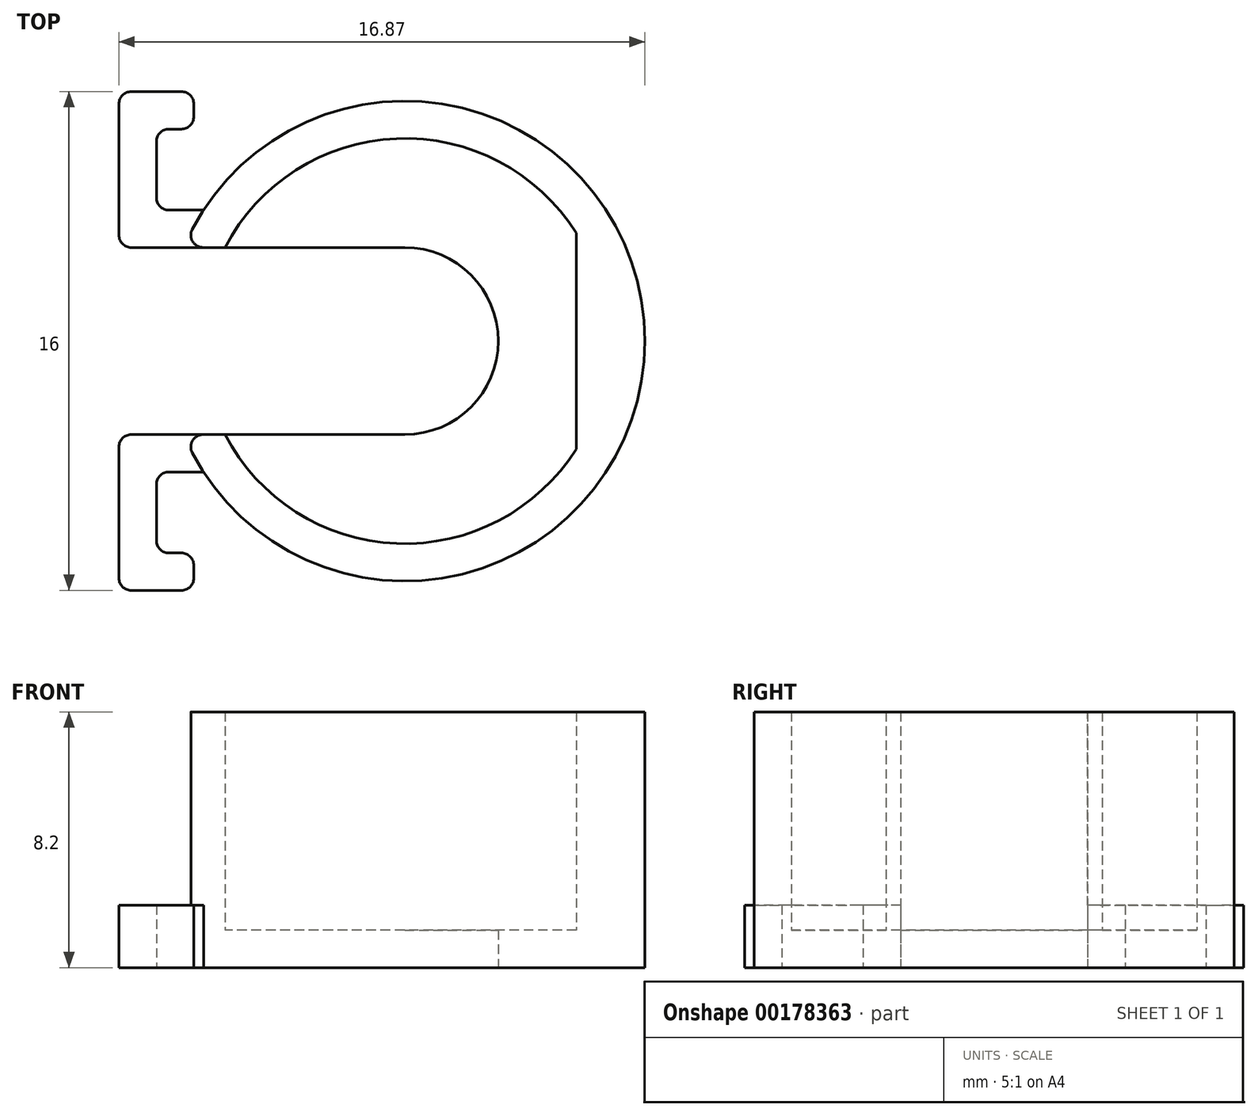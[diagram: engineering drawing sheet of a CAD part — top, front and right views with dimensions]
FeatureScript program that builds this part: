
annotation { "Feature Type Name" : "Feature", "Feature Type Description" : "" }
export const myFeature = defineFeature(function(context is Context, id is Id, definition is map)
    precondition{}
    {
        {
            var Q0;
            Q0=qCreatedBy(makeId("Top.planeOp"),FACE);
            var sketch = newSketch(context, id + "F0", { "sketchPlane" : qUnion([Q0])});
            skArc(sketch, "E0", {"start": v(-7.1, -3) * mm, "mid": v(7.7, 0) * mm, "end": v(-7.1, 3) * mm});
            skArc(sketch, "E1", {"start": v(0, -3) * mm, "mid": v(3, 0) * mm, "end": v(0, 3) * mm});
            skArc(sketch, "E2", {"start": v(-5.77, -3) * mm, "mid": v(6.5, 0) * mm, "end": v(-5.77, 3) * mm});
            skLineSegment(sketch, "E3.bottom", {"start": v(0, 3) * mm, "end": v(-10, 3) * mm});
            skLineSegment(sketch, "E3.top", {"start": v(0, -3) * mm, "end": v(-10, -3) * mm});
            skLineSegment(sketch, "E3.left", {"start": v(0, 3) * mm, "end": v(0, -3) * mm});
            skLineSegment(sketch, "E3.right", {"start": v(-10, 3) * mm, "end": v(-10, -3) * mm});
            skLineSegment(sketch, "E4", {"start": v(5.5, 3.46) * mm, "end": v(5.5, -3.46) * mm});
            skPoint(sketch, "E5.center.orphan", {"position": v(-10, 0) * mm});
            skLineSegment(sketch, "E6", {"start": v(-9.17, 3) * mm, "end": v(-9.17, 8) * mm});
            skLineSegment(sketch, "E7", {"start": v(-9.17, 8) * mm, "end": v(-7.97, 8) * mm});
            skLineSegment(sketch, "E8", {"start": v(-7.97, 6.8) * mm, "end": v(-7.97, 4.2) * mm});
            skLineSegment(sketch, "E9", {"start": v(-7.97, 4.2) * mm, "end": v(-6.45, 4.2) * mm});
            skLineSegment(sketch, "E10.MirrorCS", {"start": v(-9.17, -3) * mm, "end": v(-9.17, -8) * mm});
            skLineSegment(sketch, "E11.MirrorCS", {"start": v(-7.97, -6.8) * mm, "end": v(-7.97, -4.2) * mm});
            skLineSegment(sketch, "E12.MirrorCS", {"start": v(-7.97, -4.2) * mm, "end": v(-6.45, -4.2) * mm});
            skLineSegment(sketch, "E13.MirrorCS", {"start": v(-9.17, -8) * mm, "end": v(-7.97, -8) * mm});
            skLineSegment(sketch, "E14", {"start": v(-7.97, 8) * mm, "end": v(-6.77, 8) * mm});
            skLineSegment(sketch, "E15", {"start": v(-6.77, 8) * mm, "end": v(-6.77, 6.8) * mm});
            skLineSegment(sketch, "E16", {"start": v(-6.77, 6.8) * mm, "end": v(-7.97, 6.8) * mm});
            skLineSegment(sketch, "E17.MirrorCS", {"start": v(-6.77, -6.8) * mm, "end": v(-7.97, -6.8) * mm});
            skLineSegment(sketch, "E18.MirrorCS", {"start": v(-6.77, -8) * mm, "end": v(-6.77, -6.8) * mm});
            skLineSegment(sketch, "E19.MirrorCS", {"start": v(-7.97, -8) * mm, "end": v(-6.77, -8) * mm});
            skPoint(sketch, "E20.orphan", {"position": v(-7.97, -8) * mm});
            skSolve(sketch);
        }
        {
            var Q0;
            Q0=makeQuery(id+"F0.imprint","IMPRINT",FACE,{"disambiguationData":[TD([[makeQuery(id+"F0.imprint","IMPRINT",EDGE,{"derivedFrom":sQuery(id+"F0.wireOp",EDGE,"E0")}),1.0]])]});
            var Q1;
            {var subQ0=sQuery(id+"F0.wireOp",EDGE,"E4");Q1=makeQuery(id+"F0.imprint","IMPRINT",FACE,{"disambiguationData":[TD([[makeQuery(id+"F0.imprint","IMPRINT",EDGE,{"derivedFrom":subQ0}),1.0]])]});}
            extrude(context, id + "F1", {"entities" : qUnion([Q0, Q1]), "depth" : 8.2 * mm});
        }
        {
            var Q0;
            Q0=makeQuery(id+"F0.imprint","IMPRINT",FACE,{"disambiguationData":[TD([[makeQuery(id+"F0.imprint","IMPRINT",EDGE,{"derivedFrom":sQuery(id+"F0.wireOp",EDGE,"E1")}),-1.0]])]});
            var Q1;
            {var subQ0=sQuery(id+"F0.wireOp",EDGE,"E4");Q1=makeQuery(id+"F0.imprint","IMPRINT",FACE,{"disambiguationData":[TD([[makeQuery(id+"F0.imprint","IMPRINT",EDGE,{"derivedFrom":subQ0}),1.0]])]});}
            extrude(context, id + "F2", {"entities" : qUnion([Q0, Q1]), "operationType" : NewBodyOperationType.ADD, "depth" : 1.2 * mm});
        }
        {
            var Q0;
            {var subQ3=sQuery(id+"F0.wireOp",EDGE,"E6");Q0=makeQuery(id+"F0.imprint","IMPRINT",FACE,{"disambiguationData":[TD([[makeQuery(id+"F0.imprint","IMPRINT",EDGE,{"derivedFrom":subQ3}),-1.0]])]});}
            var Q1;
            {var subQ0=sQuery(id+"F0.wireOp",EDGE,"E10.MirrorCS");Q1=makeQuery(id+"F0.imprint","IMPRINT",FACE,{"disambiguationData":[TD([[makeQuery(id+"F0.imprint","IMPRINT",EDGE,{"derivedFrom":subQ0}),1.0]])]});}
            extrude(context, id + "F3", {"entities" : qUnion([Q0, Q1]), "operationType" : NewBodyOperationType.ADD, "depth" : 2 * mm});
        }
        {
            var Q0;
            Q0=makeQuery(id+"F3.boolean.opBoolean","SPLIT",EDGE,{"derivedFrom":makeQuery(id+"F1.opExtrude","SWEPT_EDGE",EDGE,{"disambiguationData":[OSD([sQuery(id+"F0.wireOp",EDGE,"E0"),sQuery(id+"F0.wireOp",EDGE,"E3.bottom"),sQuery(id+"F0.wireOp",EDGE,"Ywue0eLD-gD3H-Xaff-KL99-stYuEqtgMP2j")])]})});
            var Q1;
            Q1=makeQuery(id+"F3.boolean.opBoolean","SPLIT",EDGE,{"derivedFrom":makeQuery(id+"F1.opExtrude","SWEPT_EDGE",EDGE,{"disambiguationData":[OSD([sQuery(id+"F0.wireOp",EDGE,"E0"),sQuery(id+"F0.wireOp",EDGE,"E3.top"),sQuery(id+"F0.wireOp",EDGE,"pa3rI5kA-tJh4-xYh9-jey1-RvZttP9N32Lq")])]})});
            fillet(context, id + "F4", {"entities" : qUnion([Q0, Q1]), "radius" : 0.4 * mm, "tangentPropagation" : true, "allowEdgeOverflow" : false});
        }
        {
            var Q0;
            {var subQ0=sQuery(id+"F0.wireOp",EDGE,"Ywue0eLD-gD3H-Xaff-KL99-stYuEqtgMP2j");var subQ1=sQuery(id+"F0.wireOp",EDGE,"E3.bottom");var subQ2=sQuery(id+"F0.wireOp",EDGE,"E0");Q0=makeQuery(id+"F3.boolean.opBoolean","MERGE",EDGE,{"derivedFrom":[makeQuery(id+"F1.opExtrude","SWEPT_EDGE",EDGE,{"disambiguationData":[OSD([subQ2,subQ1,subQ0])]}),makeQuery(id+"F3.opExtrude","SWEPT_EDGE",EDGE,{"disambiguationData":[OSD([subQ2,subQ1,subQ0])]})]});}
            var Q1;
            {var subQ0=sQuery(id+"F0.wireOp",EDGE,"pa3rI5kA-tJh4-xYh9-jey1-RvZttP9N32Lq");var subQ1=sQuery(id+"F0.wireOp",EDGE,"E3.top");var subQ2=sQuery(id+"F0.wireOp",EDGE,"E0");Q1=makeQuery(id+"F3.boolean.opBoolean","MERGE",EDGE,{"derivedFrom":[makeQuery(id+"F1.opExtrude","SWEPT_EDGE",EDGE,{"disambiguationData":[OSD([subQ2,subQ1,subQ0])]}),makeQuery(id+"F3.opExtrude","SWEPT_EDGE",EDGE,{"disambiguationData":[OSD([subQ2,subQ1,subQ0])]})]});}
            var Q2;
            Q2=makeQuery(id+"F3.opExtrude","SWEPT_EDGE",EDGE,{"disambiguationData":[OSD([sQuery(id+"F0.wireOp",EDGE,"pa3rI5kA-tJh4-xYh9-jey1-RvZttP9N32Lq"),sQuery(id+"F0.wireOp",EDGE,"1dqWjSas-e6Ni-hklt-iOQO-hkkV1jXpteAw")])]});
            var Q3;
            Q3=makeQuery(id+"F3.opExtrude","SWEPT_EDGE",EDGE,{"disambiguationData":[OSD([sQuery(id+"F0.wireOp",EDGE,"1dqWjSas-e6Ni-hklt-iOQO-hkkV1jXpteAw"),sQuery(id+"F0.wireOp",EDGE,"BVpgv2Iz-63zP-G1oZ-N1MP-ltgHcUYc0GKi")])]});
            var Q4;
            Q4=makeQuery(id+"F3.opExtrude","SWEPT_EDGE",EDGE,{"disambiguationData":[OSD([sQuery(id+"F0.wireOp",EDGE,"Ywue0eLD-gD3H-Xaff-KL99-stYuEqtgMP2j"),sQuery(id+"F0.wireOp",EDGE,"mlycOVBG-ovkN-Ao6v-Uro5-dhjy0RPZErzt")])]});
            var Q5;
            Q5=makeQuery(id+"F3.opExtrude","SWEPT_EDGE",EDGE,{"disambiguationData":[OSD([sQuery(id+"F0.wireOp",EDGE,"mlycOVBG-ovkN-Ao6v-Uro5-dhjy0RPZErzt"),sQuery(id+"F0.wireOp",EDGE,"f3OtTEe7-KXTr-P1KM-1ql5-LDTarhRCUojX")])]});
            var Q6;
            Q6=makeQuery(id+"F3.opExtrude","SWEPT_EDGE",EDGE,{"disambiguationData":[OSD([sQuery(id+"F0.wireOp",EDGE,"E10.MirrorCS"),sQuery(id+"F0.wireOp",EDGE,"E13.MirrorCS")])]});
            var Q7;
            Q7=makeQuery(id+"F3.opExtrude","SWEPT_EDGE",EDGE,{"disambiguationData":[OSD([sQuery(id+"F0.wireOp",EDGE,"E11.MirrorCS"),sQuery(id+"F0.wireOp",EDGE,"E13.MirrorCS")])]});
            var Q8;
            Q8=makeQuery(id+"F3.opExtrude","SWEPT_EDGE",EDGE,{"disambiguationData":[OSD([sQuery(id+"F0.wireOp",EDGE,"E3.top"),sQuery(id+"F0.wireOp",EDGE,"E10.MirrorCS")])]});
            var Q9;
            Q9=makeQuery(id+"F3.opExtrude","SWEPT_EDGE",EDGE,{"disambiguationData":[OSD([sQuery(id+"F0.wireOp",EDGE,"E3.bottom"),sQuery(id+"F0.wireOp",EDGE,"E6")])]});
            var Q10;
            Q10=makeQuery(id+"F3.opExtrude","SWEPT_EDGE",EDGE,{"disambiguationData":[OSD([sQuery(id+"F0.wireOp",EDGE,"E6"),sQuery(id+"F0.wireOp",EDGE,"E7")])]});
            var Q11;
            Q11=makeQuery(id+"F3.opExtrude","SWEPT_EDGE",EDGE,{"disambiguationData":[OSD([sQuery(id+"F0.wireOp",EDGE,"E7"),sQuery(id+"F0.wireOp",EDGE,"E8")])]});
            var Q12;
            Q12=makeQuery(id+"F3.opExtrude","SWEPT_EDGE",EDGE,{"disambiguationData":[OSD([sQuery(id+"F0.wireOp",EDGE,"E8"),sQuery(id+"F0.wireOp",EDGE,"E9")])]});
            var Q13;
            Q13=makeQuery(id+"F3.opExtrude","SWEPT_EDGE",EDGE,{"disambiguationData":[OSD([sQuery(id+"F0.wireOp",EDGE,"E0"),sQuery(id+"F0.wireOp",EDGE,"E9")])]});
            var Q14;
            Q14=makeQuery(id+"F3.opExtrude","SWEPT_EDGE",EDGE,{"disambiguationData":[OSD([sQuery(id+"F0.wireOp",EDGE,"E0"),sQuery(id+"F0.wireOp",EDGE,"E12.MirrorCS")])]});
            var Q15;
            Q15=makeQuery(id+"F3.opExtrude","SWEPT_EDGE",EDGE,{"disambiguationData":[OSD([sQuery(id+"F0.wireOp",EDGE,"E11.MirrorCS"),sQuery(id+"F0.wireOp",EDGE,"E12.MirrorCS")])]});
            var Q16;
            Q16=makeQuery(id+"F3.opExtrude","SWEPT_EDGE",EDGE,{"disambiguationData":[OSD([sQuery(id+"F0.wireOp",EDGE,"E15"),sQuery(id+"F0.wireOp",EDGE,"E16")])]});
            var Q17;
            Q17=makeQuery(id+"F3.opExtrude","SWEPT_EDGE",EDGE,{"disambiguationData":[OSD([sQuery(id+"F0.wireOp",EDGE,"E18.MirrorCS"),sQuery(id+"F0.wireOp",EDGE,"E19.MirrorCS")])]});
            var Q18;
            Q18=makeQuery(id+"F3.opExtrude","SWEPT_EDGE",EDGE,{"disambiguationData":[OSD([sQuery(id+"F0.wireOp",EDGE,"E17.MirrorCS"),sQuery(id+"F0.wireOp",EDGE,"E18.MirrorCS")])]});
            var Q19;
            Q19=makeQuery(id+"F3.opExtrude","SWEPT_EDGE",EDGE,{"disambiguationData":[OSD([sQuery(id+"F0.wireOp",EDGE,"E14"),sQuery(id+"F0.wireOp",EDGE,"E15")])]});
            fillet(context, id + "F5", {"entities" : qUnion([Q0, Q1, Q2, Q3, Q4, Q5, Q6, Q7, Q8, Q9, Q10, Q11, Q12, Q13, Q14, Q15, Q16, Q17, Q18, Q19]), "radius" : 0.4 * mm, "tangentPropagation" : true, "allowEdgeOverflow" : false});
        }
    });
